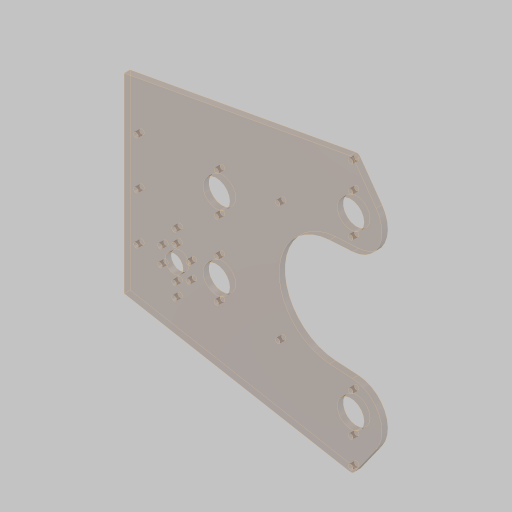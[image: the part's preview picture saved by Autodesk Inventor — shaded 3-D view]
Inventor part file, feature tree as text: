
AUTODESK INVENTOR PART (.ipt)
format: ipt  version: 2023.5 (Build 275446000, 446)  size: 200,704 bytes
history: native  units: in
note: dims shown in document units (in); Inventor stores cm internally (conversion verified against a paired STEP export)
features: sketch x1, extrude x1, hole x1
ambient origin geometry x8: Origin, YZ Plane, XZ Plane, XY Plane, X Axis, Y Axis, Z Axis, Center Point
bodies: Solid1 (feature_tree)
feature tree (3):
  sketch  "Sketch1"  dims[d0=3.0in d1=3.0in d2=4.5in d4=7.2284in d5=1.125in d6=0.75in d7=1.128in d8=1.88in d9=3.125in d10=5.6298in d11=5.992in d12=1.125in d13=0.4688in d14=0.75in d15=1.375in d16=2.3622in d18=360.0deg d20=0.25in d21=1.5in d22=1.0in d23=8.0in d24=9.5in d26=5.0in d27=0.25in d28=0.0in d29=0.375in d30=0.25in d32=1.655in d33=1.655in d34=1.655in d35=1.655in d36=1.0in d37=0.201in d38=0.75in d39=0.385in d40=0.25in d41=0.5635in d42=1.0in d43=0.8108in d44=4.0in d45=2.5in d47=0.375in d49=2.125in]
  extrude  "Extrusion1"  Depth=0.375in
  hole  "Hole1"  [1 undecoded]
note: 1 required parameter value undecoded (feature->parameter linkage not recoverable at this tier; creation-order binding heuristic only, values carry confidence <= 0.55)
